# Revit family: PlumFix_Mixer_ABEY_Poco_Wall Basin-Bath Set_165mm_Face Based
name_source: partatom
category: Plumbing Fixtures
revit_build: Autodesk Revit 2016 (Build: 20150220_1215(x64)
units: mm (PartAtom-declared; Revit-internal decimal feet)

## family parameters
Cut with Voids When Loaded = Yes
Host = Face
OmniClass Number = 23.45.55.17
OmniClass Title = Mixing Faucets
Part Type = Normal
Room Calculation Point = No
Round Connector Dimension = Use Diameter
Shared = No

## types (1)
- Chrome
    Assembly Code = 0.00
    BodyMaterial = z_Abey_Chrome
    CW Connection = Yes
    Default Elevation = 900 mm  [stored 2.95276 ft]
    Description = Poco - Wall Basin/Bath Set 165mm - Chrome
    HW Connection = Yes
    Manufacturer = Abey Australia
    Manufacturer_Overall Depth = 119 mm  [stored 0.39042 ft]
    Manufacturer_Overall Height = 174 mm
    Manufacturer_Overall Width = 172 mm
    Manufacturer_Spec Code = 6B-WS165
    Manufacturer_URL__Product Specific = https://www.abey.com.au
    Model = 6B-WS165
    ModifiedIssue_ANZRS = 20190823 $
    Type Comments = Chrome Finish
    URL = https://www.abey.com.au
    Vent Connection = No
    Waste Connection = No

note: [stored X ft] marks values corroborated as IEEE doubles in the binary element streams (Revit-internal decimal feet)

## geometry (parser evidence)
native form markers: Sweep x5
no freeform markers — native parametric forms only
